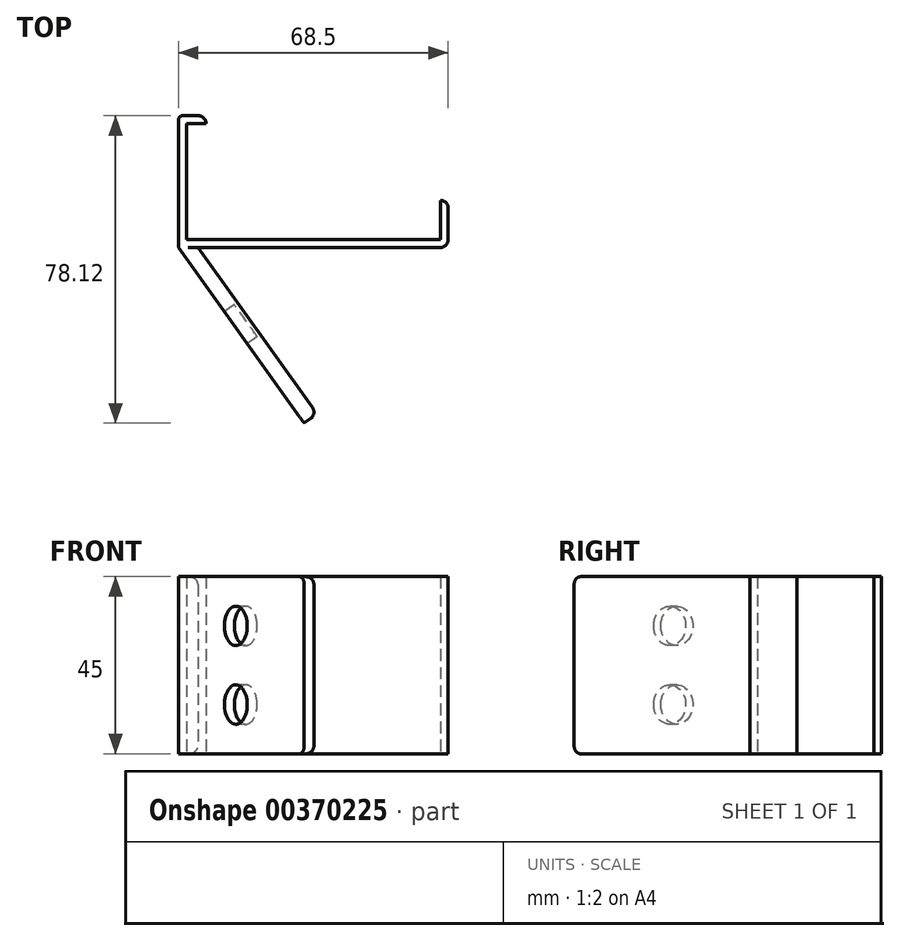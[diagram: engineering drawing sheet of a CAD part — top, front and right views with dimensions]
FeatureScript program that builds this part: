
annotation { "Feature Type Name" : "Feature", "Feature Type Description" : "" }
export const myFeature = defineFeature(function(context is Context, id is Id, definition is map)
    precondition{}
    {
        {
            var Q0;
            Q0=qCreatedBy(makeId("Top.planeOp"),FACE);
            var sketch = newSketch(context, id + "F0", { "sketchPlane" : qUnion([Q0])});
            skLineSegment(sketch, "E0", {"start": v(0, 0) * mm, "end": v(30.25, -42.3) * mm});
            skLineSegment(sketch, "E1", {"start": v(30.25, -42.3) * mm, "end": v(27, -44.62) * mm});
            skLineSegment(sketch, "E2", {"start": v(27, -44.62) * mm, "end": v(-4.92, 0) * mm});
            skLineSegment(sketch, "E3", {"start": v(-2.92, 2) * mm, "end": v(61.58, 2) * mm});
            skLineSegment(sketch, "E4", {"start": v(61.58, 2) * mm, "end": v(61.58, 12) * mm});
            skLineSegment(sketch, "E5", {"start": v(61.58, 12) * mm, "end": v(63.58, 12) * mm});
            skLineSegment(sketch, "E6", {"start": v(63.58, 12) * mm, "end": v(63.58, 0) * mm});
            skLineSegment(sketch, "E7", {"start": v(63.58, 0) * mm, "end": v(0, 0) * mm});
            skLineSegment(sketch, "E8", {"start": v(-2.92, 2) * mm, "end": v(-2.92, 31.5) * mm});
            skLineSegment(sketch, "E9", {"start": v(-4.92, 31.5) * mm, "end": v(-4.92, 0) * mm});
            skLineSegment(sketch, "E10", {"start": v(-2.92, 31.5) * mm, "end": v(2.08, 31.5) * mm});
            skLineSegment(sketch, "E11", {"start": v(2.08, 31.5) * mm, "end": v(2.08, 33.5) * mm});
            skLineSegment(sketch, "E12", {"start": v(2.08, 33.5) * mm, "end": v(-4.92, 33.5) * mm});
            skLineSegment(sketch, "E13", {"start": v(-4.92, 33.5) * mm, "end": v(-4.92, 31.5) * mm});
            skSolve(sketch);
        }
        {
            var Q0;
            Q0=makeQuery(id+"F0.imprint","IMPRINT",FACE,{"disambiguationData":[TD([[makeQuery(id+"F0.imprint","IMPRINT",EDGE,{"derivedFrom":sQuery(id+"F0.wireOp",EDGE,"E0")}),-1.0]])]});
            extrude(context, id + "F1", {"entities" : qUnion([Q0]), "depth" : 45 * mm});
        }
        {
            var Q0;
            Q0=makeQuery(id+"F1.opExtrude","SWEPT_EDGE",EDGE,{"disambiguationData":[OSD([sQuery(id+"F0.wireOp",EDGE,"E6"),sQuery(id+"F0.wireOp",EDGE,"E7")])]});
            var Q1;
            Q1=makeQuery(id+"F1.opExtrude","SWEPT_EDGE",EDGE,{"disambiguationData":[OSD([sQuery(id+"F0.wireOp",EDGE,"E5"),sQuery(id+"F0.wireOp",EDGE,"E6")])]});
            var Q2;
            Q2=makeQuery(id+"F1.opExtrude","SWEPT_EDGE",EDGE,{"disambiguationData":[OSD([sQuery(id+"F0.wireOp",EDGE,"M2ZkYjIz-Av6z-WNUJ-o27c-PJpOkU5waALy"),sQuery(id+"F0.wireOp",EDGE,"etDyBB0R-myPZ-BQgV-93i8-wXP0kOZwynyK")])]});
            var Q3;
            Q3=makeQuery(id+"F1.opExtrude","SWEPT_EDGE",EDGE,{"disambiguationData":[OSD([sQuery(id+"F0.wireOp",EDGE,"E0"),sQuery(id+"F0.wireOp",EDGE,"E1")])]});
            var Q4;
            Q4=makeQuery(id+"F1.opExtrude","CAP_EDGE",EDGE,{"disambiguationData":[OSD([sQuery(id+"F0.wireOp",EDGE,"E1")])],"isStart":false});
            var Q5;
            Q5=makeQuery(id+"F1.opExtrude","CAP_EDGE",EDGE,{"disambiguationData":[OSD([sQuery(id+"F0.wireOp",EDGE,"E1")])],"isStart":true});
            var Q6;
            Q6=makeQuery(id+"F1.opExtrude","CAP_EDGE",EDGE,{"disambiguationData":[OSD([sQuery(id+"F0.wireOp",EDGE,"E0")])],"isStart":false});
            var Q7;
            Q7=makeQuery(id+"F1.opExtrude","CAP_EDGE",EDGE,{"disambiguationData":[OSD([sQuery(id+"F0.wireOp",EDGE,"E0")])],"isStart":true});
            var Q8;
            Q8=makeQuery(id+"F1.opExtrude","SWEPT_EDGE",EDGE,{"disambiguationData":[OSD([sQuery(id+"F0.wireOp",EDGE,"E11"),sQuery(id+"F0.wireOp",EDGE,"E12")])]});
            fillet(context, id + "F2", {"entities" : qUnion([Q0, Q1, Q2, Q3, Q4, Q5, Q6, Q7, Q8]), "radius" : 2 * mm, "tangentPropagation" : true, "allowEdgeOverflow" : false});
        }
        {
            var Q0;
            Q0=makeQuery(id+"F1.opExtrude","SWEPT_FACE",FACE,{"disambiguationData":[OSD([sQuery(id+"F0.wireOp",EDGE,"E2")])]});
            var sketch = newSketch(context, id + "F3", { "sketchPlane" : qUnion([Q0])});
            skCircle(sketch, "E14", {"center": v(22.14, 32.5) * mm, "radius": 5 * mm});
            skCircle(sketch, "E15", {"center": v(22.14, 12.5) * mm, "radius": 5 * mm});
            skSolve(sketch);
        }
        {
            var Q0;
            Q0=makeQuery(id+"F1.opExtrude","SWEPT_EDGE",EDGE,{"disambiguationData":[OSD([sQuery(id+"F0.wireOp",EDGE,"E12"),sQuery(id+"F0.wireOp",EDGE,"E13")])]});
            fillet(context, id + "F4", {"entities" : qUnion([Q0]), "radius" : 1 * mm, "tangentPropagation" : true, "allowEdgeOverflow" : false});
        }
        {
            var Q0;
            Q0=makeQuery(id+"F3.imprint","IMPRINT",FACE,{"disambiguationData":[TD([[makeQuery(id+"F3.imprint","IMPRINT",EDGE,{"derivedFrom":sQuery(id+"F3.wireOp",EDGE,"E15")}),1.0]])]});
            var Q1;
            Q1=makeQuery(id+"F3.imprint","IMPRINT",FACE,{"disambiguationData":[TD([[makeQuery(id+"F3.imprint","IMPRINT",EDGE,{"derivedFrom":sQuery(id+"F3.wireOp",EDGE,"E14")}),1.0]])]});
            extrude(context, id + "F5", {"entities" : qUnion([Q0, Q1]), "operationType" : NewBodyOperationType.REMOVE, "oppositeDirection" : true, "depth" : 3.1 * mm, "offsetDistance" : 25 * mm});
        }
    });
